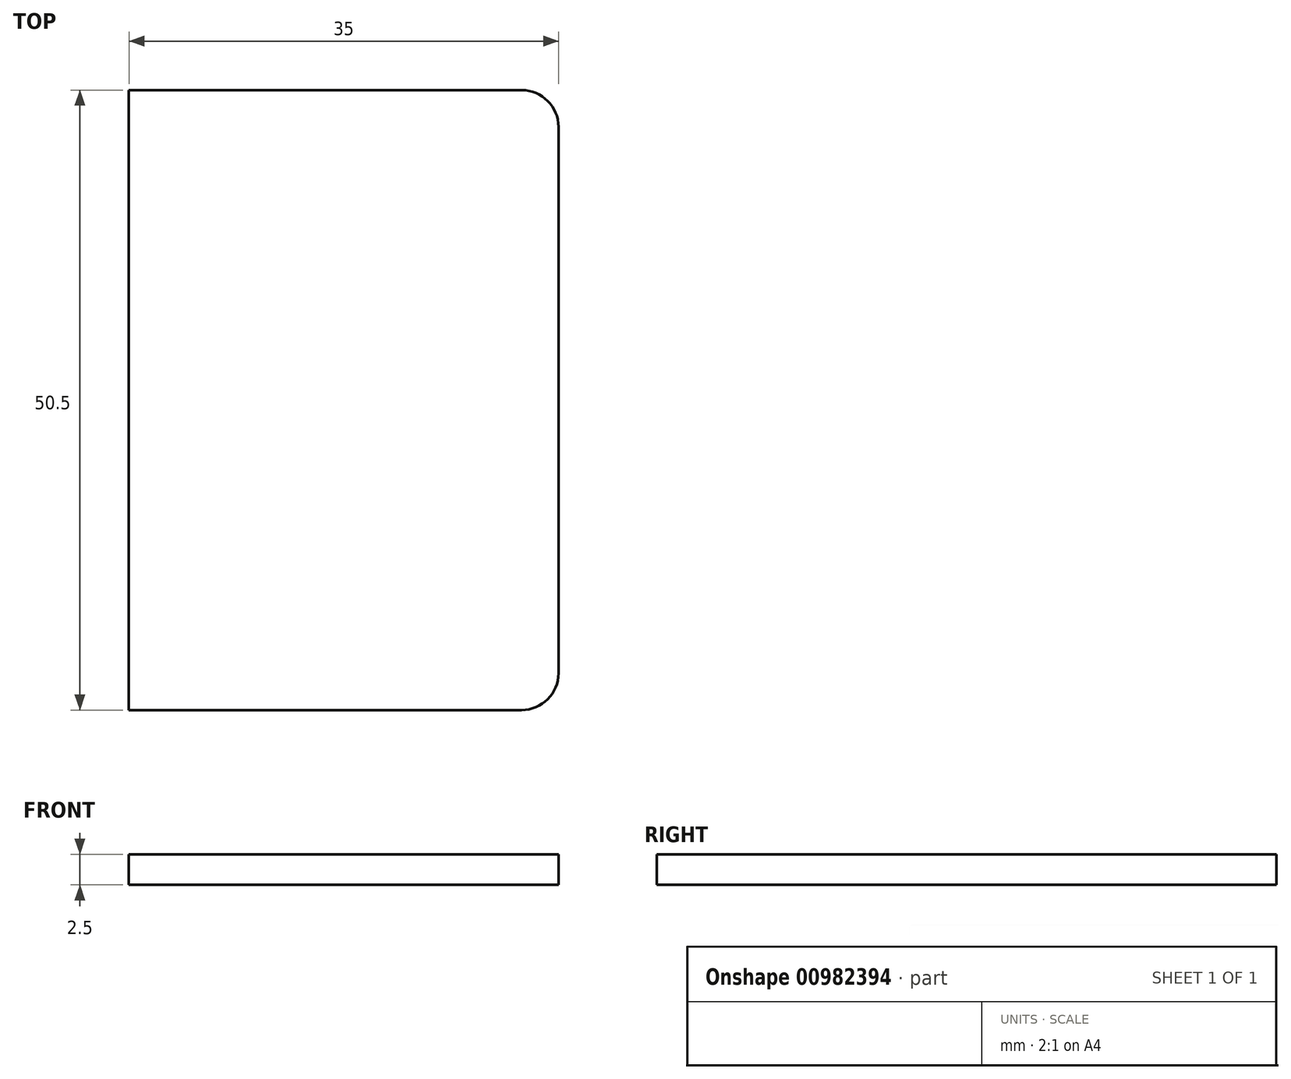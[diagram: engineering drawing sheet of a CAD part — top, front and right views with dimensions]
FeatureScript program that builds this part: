
annotation { "Feature Type Name" : "Feature", "Feature Type Description" : "" }
export const myFeature = defineFeature(function(context is Context, id is Id, definition is map)
    precondition{}
    {
        {
            var Q0;
            Q0=qCreatedBy(makeId("Top.planeOp"),FACE);
            var sketch = newSketch(context, id + "F0", { "sketchPlane" : qUnion([Q0])});
            skLineSegment(sketch, "E0.bottom", {"start": v(-26.41, 8.9) * mm, "end": v(5.59, 8.9) * mm});
            skLineSegment(sketch, "E0.top", {"start": v(-26.41, -41.6) * mm, "end": v(5.59, -41.6) * mm});
            skLineSegment(sketch, "E0.left", {"start": v(-26.41, 8.9) * mm, "end": v(-26.41, -41.6) * mm});
            skLineSegment(sketch, "E0.right", {"start": v(8.59, 5.9) * mm, "end": v(8.59, -38.6) * mm});
            skPoint(sketch, "E1.visualSharp", {"position": v(8.59, 8.9) * mm});
            skArc(sketch, "E1.filletArc", {"start": v(8.59, 5.9) * mm, "mid": v(7.7, 8.01) * mm, "end": v(5.59, 8.9) * mm});
            skPoint(sketch, "E2.visualSharp", {"position": v(8.59, -41.6) * mm});
            skArc(sketch, "E2.filletArc", {"start": v(5.59, -41.6) * mm, "mid": v(7.7, -40.73) * mm, "end": v(8.59, -38.6) * mm});
            skSolve(sketch);
        }
        {
            var Q0;
            Q0=makeQuery(id+"F0.imprint","IMPRINT",FACE,{"disambiguationData":[TD([[makeQuery(id+"F0.imprint","IMPRINT",EDGE,{"derivedFrom":sQuery(id+"F0.wireOp",EDGE,"E0.bottom")}),-1.0]])]});
            extrude(context, id + "F1", {"entities" : qUnion([Q0]), "depth" : 2.5 * mm, "offsetDistance" : 25 * mm});
        }
    });
